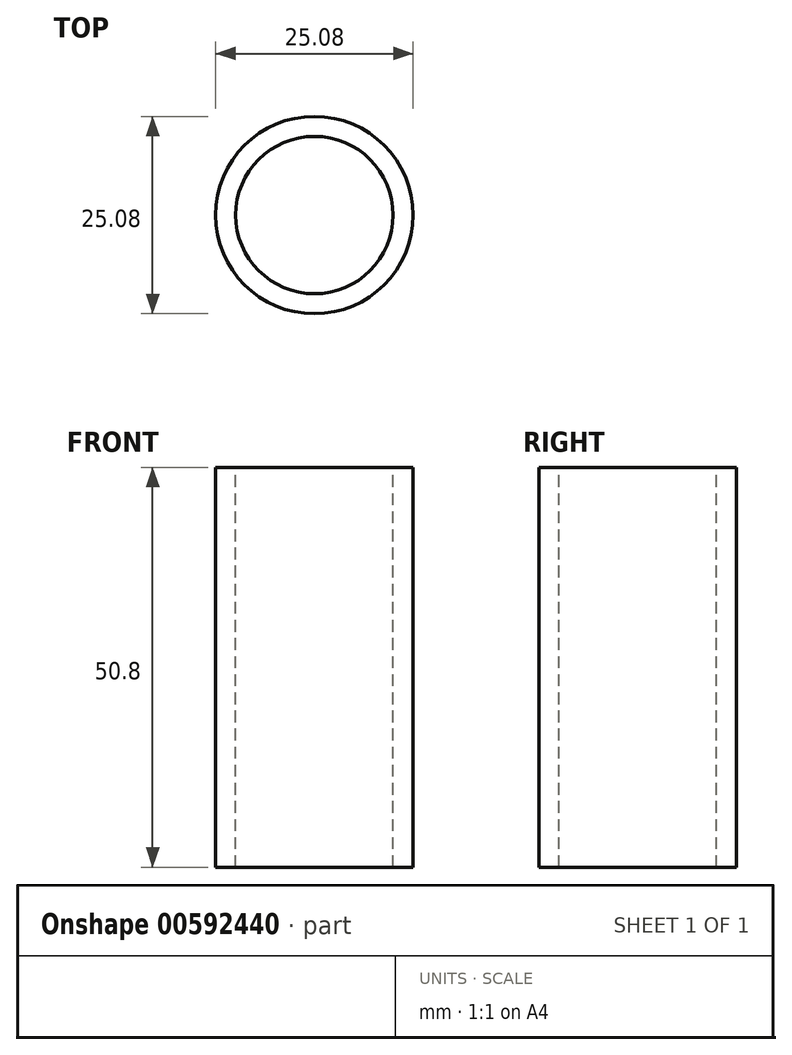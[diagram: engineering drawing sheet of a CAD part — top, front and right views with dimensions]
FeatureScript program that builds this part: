
annotation { "Feature Type Name" : "Feature", "Feature Type Description" : "" }
export const myFeature = defineFeature(function(context is Context, id is Id, definition is map)
    precondition{}
    {
        {
            var Q0;
            Q0=qCreatedBy(makeId("Top.planeOp"),FACE);
            var sketch = newSketch(context, id + "F0", { "sketchPlane" : qUnion([Q0])});
            skCircle(sketch, "E0", {"center": v(0, 0) * mm, "radius": 10 * mm});
            skCircle(sketch, "E1.0", {"center": v(0, 0) * mm, "radius": 12.54 * mm});
            skSolve(sketch);
        }
        {
            var Q0;
            Q0 = qConstructionFilter(qBodyType(qCreatedBy(id + "F0" ,EDGE), BodyType.WIRE), ConstructionObject.NO);
            extrude(context, id + "F1", {"bodyType" : ToolBodyType.SURFACE, "surfaceEntities" : qUnion([Q0]), "depth" : 50.8 * mm, "offsetDistance" : 25.4 * mm});
        }
    });
